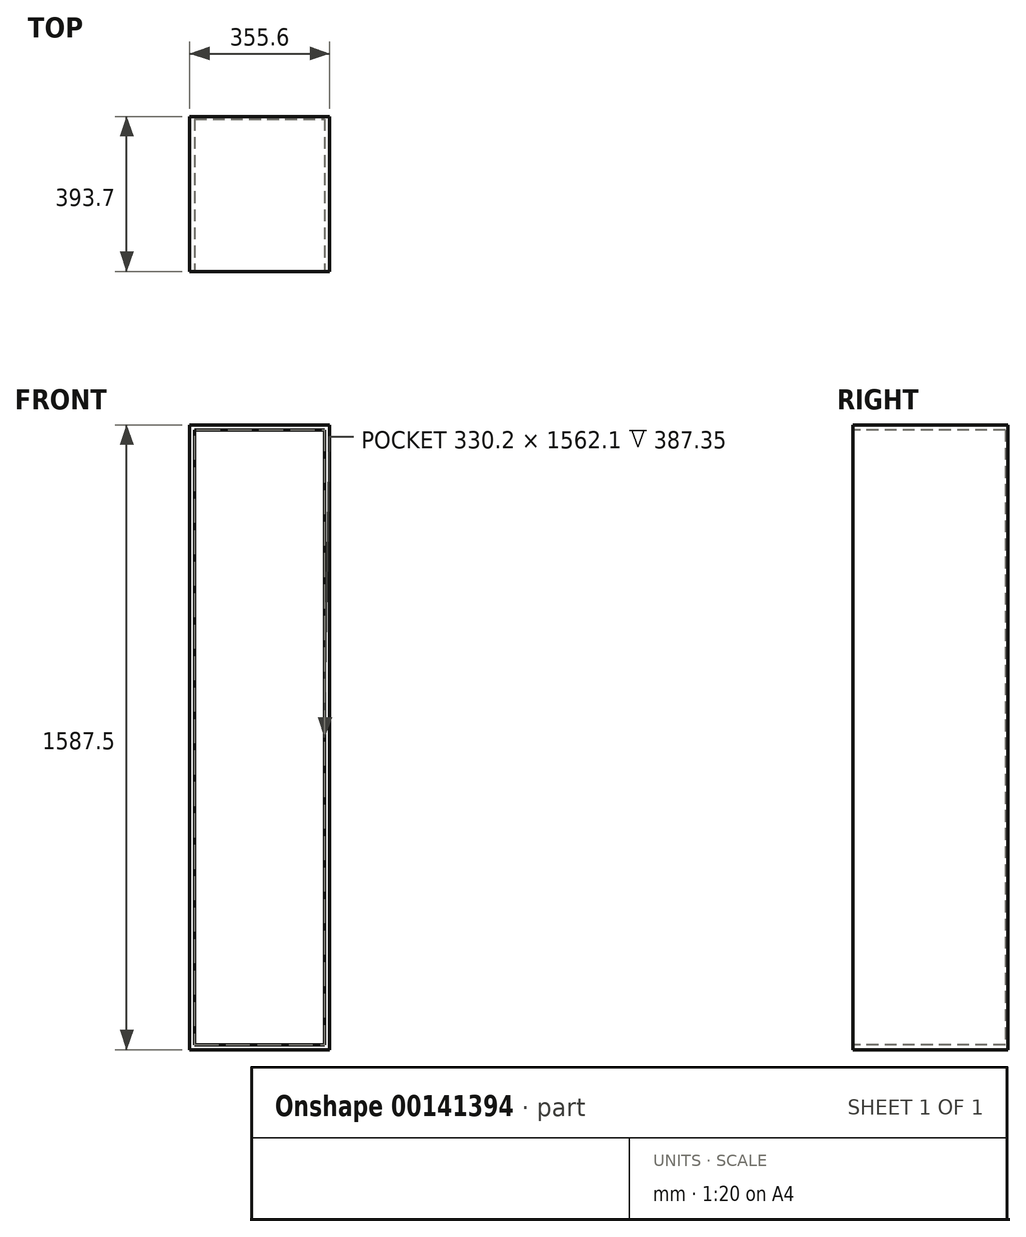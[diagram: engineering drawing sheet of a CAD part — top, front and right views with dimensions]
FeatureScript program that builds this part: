
annotation { "Feature Type Name" : "Feature", "Feature Type Description" : "" }
export const myFeature = defineFeature(function(context is Context, id is Id, definition is map)
    precondition{}
    {
        {
            var Q0;
            Q0=qCreatedBy(makeId("Top.planeOp"),FACE);
            var sketch = newSketch(context, id + "F0", { "sketchPlane" : qUnion([Q0])});
            skLineSegment(sketch, "E0.bottom", {"start": v(-177.8, 196.85) * mm, "end": v(177.8, 196.85) * mm});
            skLineSegment(sketch, "E0.top", {"start": v(-177.8, -196.85) * mm, "end": v(177.8, -196.85) * mm});
            skLineSegment(sketch, "E0.left", {"start": v(-177.8, 196.85) * mm, "end": v(-177.8, -196.85) * mm});
            skLineSegment(sketch, "E0.right", {"start": v(177.8, 196.85) * mm, "end": v(177.8, -196.85) * mm});
            skPoint(sketch, "E0.middle", {"position": v(0, 0) * mm});
            skSolve(sketch);
        }
        {
            var Q0;
            Q0 = qSketchRegion(id + "F0", true);
            extrude(context, id + "F1", {"entities" : qUnion([Q0]), "depth" : 1587.5 * mm});
        }
        {
            var Q0;
            Q0=makeQuery(id+"F1.opExtrude","SWEPT_FACE",FACE,{"disambiguationData":[OSD([sQuery(id+"F0.wireOp",EDGE,"E0.top")])]});
            var sketch = newSketch(context, id + "F2", { "sketchPlane" : qUnion([Q0])});
            skLineSegment(sketch, "E1.bottom", {"start": v(-165.1, 1574.8) * mm, "end": v(165.1, 1574.8) * mm});
            skLineSegment(sketch, "E1.top", {"start": v(-165.1, 12.7) * mm, "end": v(165.1, 12.7) * mm});
            skLineSegment(sketch, "E1.left", {"start": v(-165.1, 1574.8) * mm, "end": v(-165.1, 12.7) * mm});
            skLineSegment(sketch, "E1.right", {"start": v(165.1, 1574.8) * mm, "end": v(165.1, 12.7) * mm});
            skSolve(sketch);
        }
        {
            var Q0;
            Q0=makeQuery(id+"F2.imprint","IMPRINT",FACE,{"disambiguationData":[TD([[makeQuery(id+"F2.imprint","IMPRINT",EDGE,{"derivedFrom":sQuery(id+"F2.wireOp",EDGE,"E1.bottom")}),-1.0]])]});
            extrude(context, id + "F3", {"entities" : qUnion([Q0]), "operationType" : NewBodyOperationType.REMOVE, "oppositeDirection" : true, "depth" : 387.35 * mm});
        }
    });
